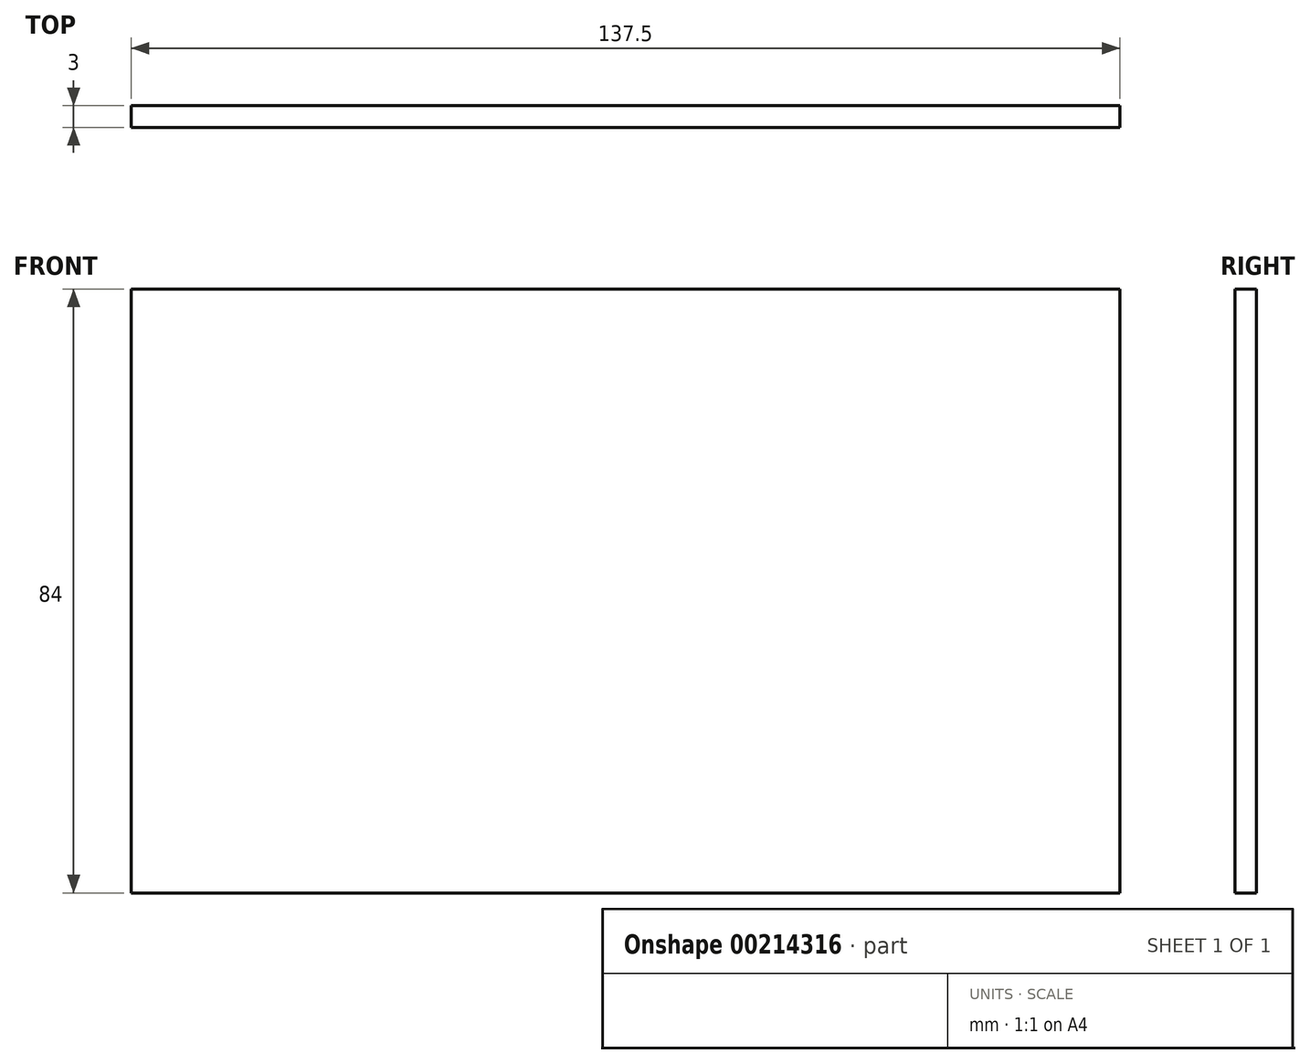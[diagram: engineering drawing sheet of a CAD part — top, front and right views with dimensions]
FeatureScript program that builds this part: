
annotation { "Feature Type Name" : "Feature", "Feature Type Description" : "" }
export const myFeature = defineFeature(function(context is Context, id is Id, definition is map)
    precondition{}
    {
        {
            var Q0;
            Q0=qCreatedBy(makeId("Front.planeOp"),FACE);
            var sketch = newSketch(context, id + "F0", { "sketchPlane" : qUnion([Q0])});
            skLineSegment(sketch, "E0.bottom", {"start": v(68.75, 42) * mm, "end": v(-68.75, 42) * mm});
            skLineSegment(sketch, "E0.top", {"start": v(68.75, -42) * mm, "end": v(-68.75, -42) * mm});
            skLineSegment(sketch, "E0.left", {"start": v(68.75, 42) * mm, "end": v(68.75, -42) * mm});
            skLineSegment(sketch, "E0.right", {"start": v(-68.75, 42) * mm, "end": v(-68.75, -42) * mm});
            skPoint(sketch, "E0.middle", {"position": v(0, 0) * mm});
            skSolve(sketch);
        }
        {
            var Q0;
            Q0 = qSketchRegion(id + "F0", true);
            extrude(context, id + "F1", {"entities" : qUnion([Q0]), "depth" : 3 * mm, "offsetDistance" : 25 * mm});
        }
    });
